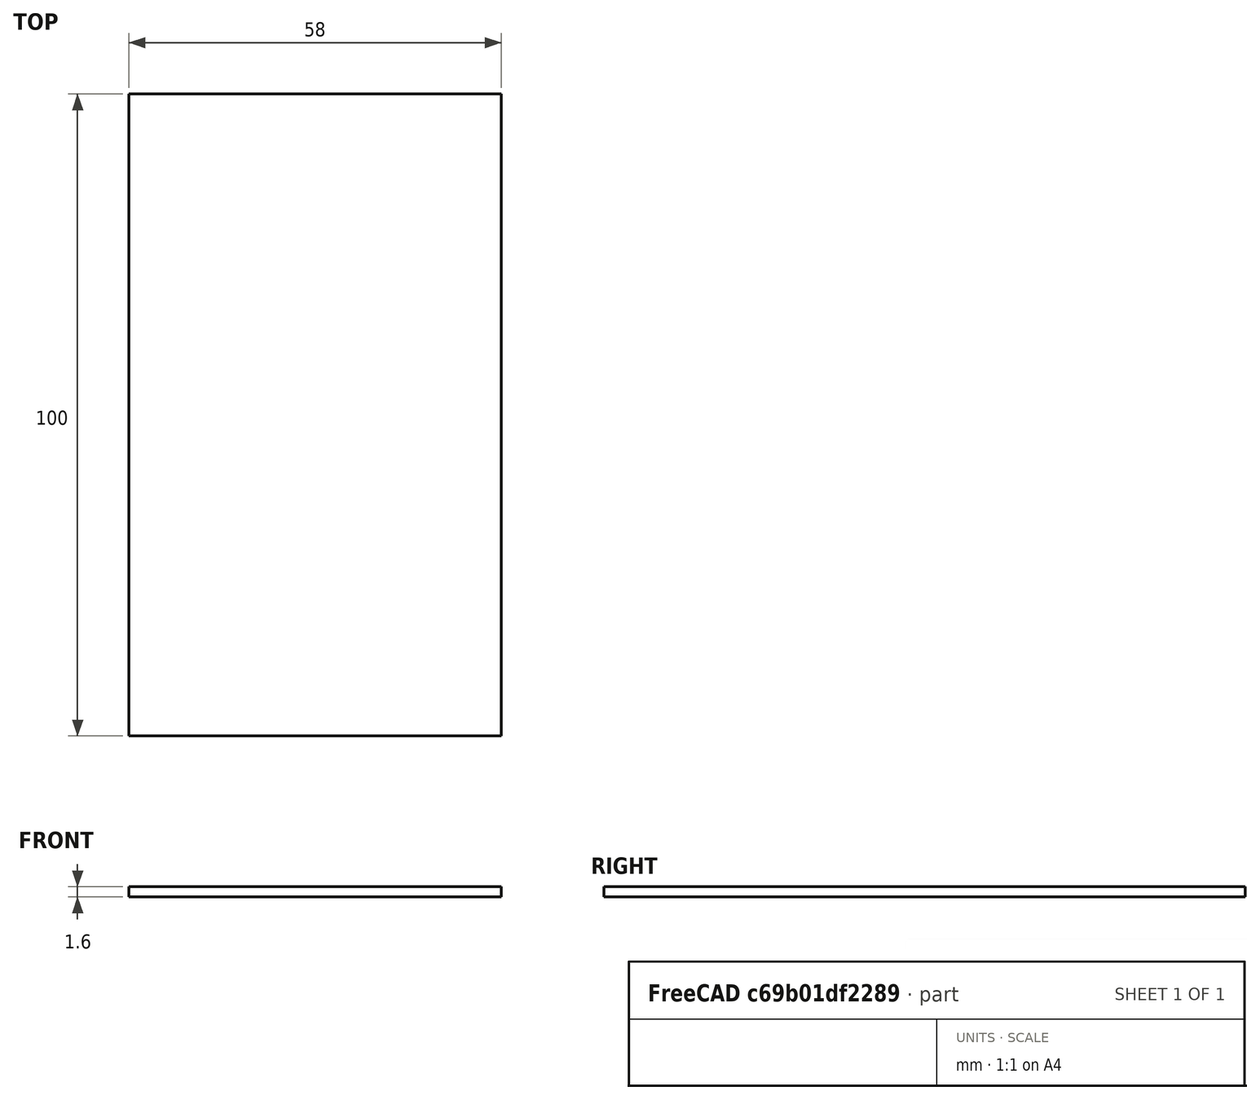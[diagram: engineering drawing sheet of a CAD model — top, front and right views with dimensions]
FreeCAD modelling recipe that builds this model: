
FCSTD DOCUMENT  (FreeCAD 0.20R29603 (Git))
Label: PCB_Chanel_58x100
License: All rights reserved
LicenseURL: http://en.wikipedia.org/wiki/All_rights_reserved
objects: Sketcher::SketchObject×1, PartDesign::Pad×1, PartDesign::Body×1
note: 4 computed .brp shape members not serialized (recipe doc carries the construction recipe); baked Part::Feature solids carry a one-line shape summary decoded from their .brp

FEATURE [Sketcher::SketchObject] Sketch
  FullyConstrained = true
  MapMode = 5
  Support = -> [XY_Plane]
  sketch-geometry (4):
    g0: LineSegment StartX=0 StartY=0 StartZ=0 EndX=58 EndY=0 EndZ=0
    g1: LineSegment StartX=58 StartY=0 StartZ=0 EndX=58 EndY=100 EndZ=0
    g2: LineSegment StartX=58 StartY=100 StartZ=0 EndX=0 EndY=100 EndZ=0
    g3: LineSegment StartX=0 StartY=100 StartZ=0 EndX=0 EndY=0 EndZ=0
  constraints (11):
    c: Coincident(g0,g1)
    c: Coincident(g1,g2)
    c: Coincident(g2,g3)
    c: Coincident(g3,g0)
    c: Horizontal(g0)
    c: Horizontal(g2)
    c: Vertical(g1)
    c: Vertical(g3)
    c: Coincident(g0,g-1)
    c: DistanceY(g3,g3) = 100
    c: DistanceX(g0,g0) = 58
FEATURE [PartDesign::Pad] Pad
  Direction = (0,0,1)
  Length = 1.6
  Length2 = 10
  Profile = -> Sketch
  ReferenceAxis = -> Sketch [N_Axis]
  Type = 0
FEATURE [PartDesign::Body] Body
  Group = -> [Sketch,Pad]
  Origin = -> Origin
  Tip = -> Pad
